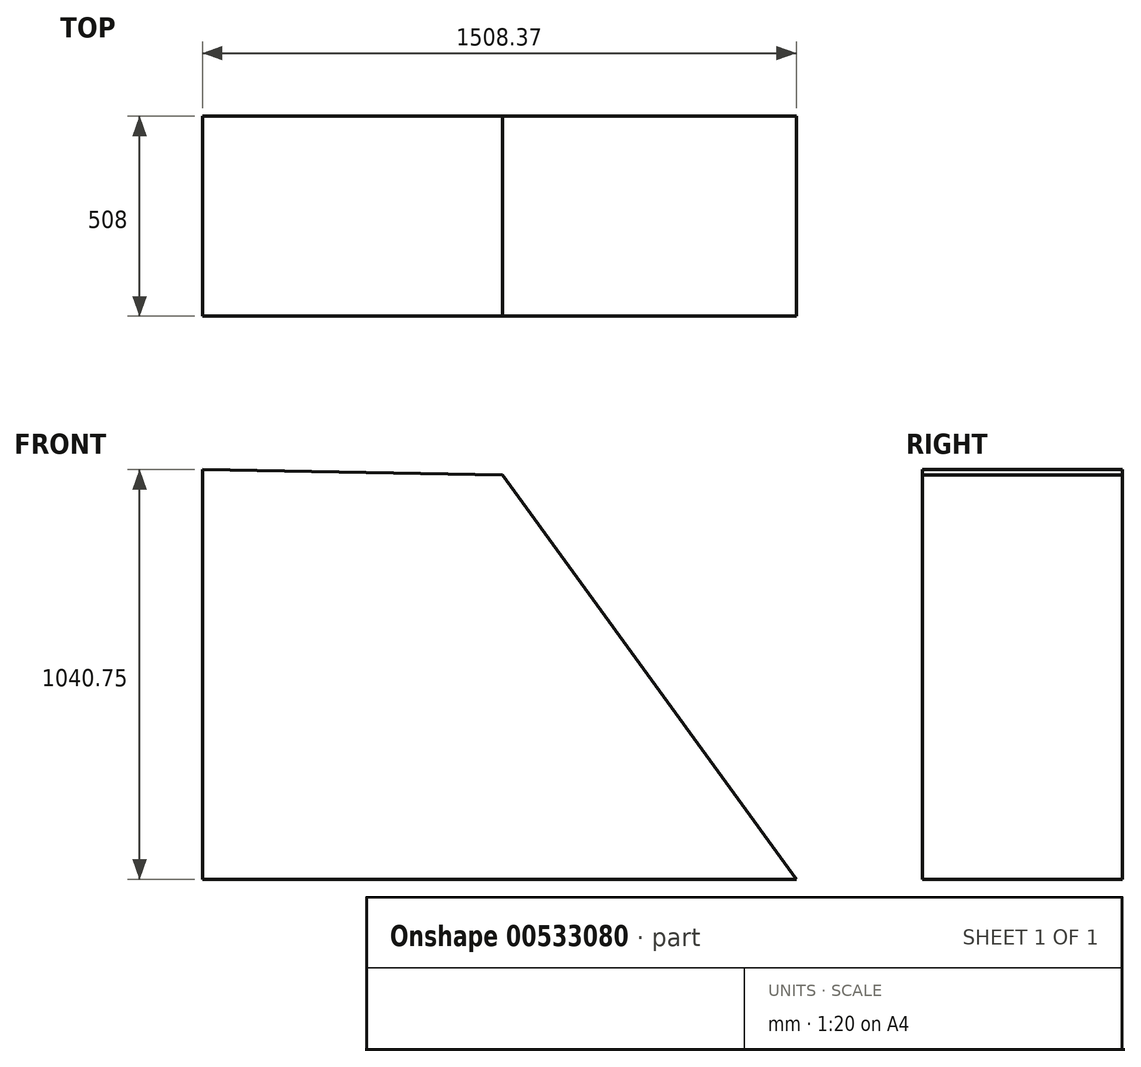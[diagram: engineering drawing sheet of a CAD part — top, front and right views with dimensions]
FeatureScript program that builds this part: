
annotation { "Feature Type Name" : "Feature", "Feature Type Description" : "" }
export const myFeature = defineFeature(function(context is Context, id is Id, definition is map)
    precondition{}
    {
        {
            var Q0;
            Q0=qCreatedBy(makeId("Front.planeOp"),FACE);
            var sketch = newSketch(context, id + "F0", { "sketchPlane" : qUnion([Q0])});
            skLineSegment(sketch, "E0", {"start": v(0, 0) * mm, "end": v(1508.37, 0) * mm});
            skLineSegment(sketch, "E1", {"start": v(1508.37, 0) * mm, "end": v(761.88, 1027.45) * mm});
            skLineSegment(sketch, "E2", {"start": v(761.88, 1027.45) * mm, "end": v(0, 1040.75) * mm});
            skLineSegment(sketch, "E3", {"start": v(0, 1040.75) * mm, "end": v(0, 0) * mm});
            skSolve(sketch);
        }
        {
            var Q0;
            Q0=makeQuery(id+"F0.imprint","IMPRINT",FACE,{"disambiguationData":[TD([[makeQuery(id+"F0.imprint","IMPRINT",EDGE,{"derivedFrom":sQuery(id+"F0.wireOp",EDGE,"E0")}),1.0]])]});
            extrude(context, id + "F1", {"entities" : qUnion([Q0]), "depth" : 508 * mm, "offsetDistance" : 25.4 * mm});
        }
    });
